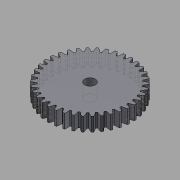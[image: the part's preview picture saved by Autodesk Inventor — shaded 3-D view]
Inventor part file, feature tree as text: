
AUTODESK INVENTOR PART (.ipt)
format: ipt  version: 2015 (Build 190159000, 159)  size: 326,656 bytes
history: native  units: in
note: dims shown in document units (in); Inventor stores cm internally (conversion verified against a paired STEP export)
features: other x13, sketch x3, plane x2
ambient origin geometry x8: Origin, YZ Plane, XZ Plane, XY Plane, X Axis, Y Axis, Z Axis, Center Point
bodies: Solid1 (feature_tree)
feature tree (18):
  other  "Spur Gear2"
  other  "Solid1::Spur Gear2"
  other  "TaggingFeature1"
  sketch  "Sketch1"  dims[d0=0.3937in]
  sketch  "Sketch2"  dims[d16=0.4724in d17=0.0in d41=0.0in d43=0.4724in d46=0.4724in d47=0.0in d48=0.0in]
  sketch  "Sketch3"
  plane  "XZ Plane_1"
  plane  "Work Plane2"
  other  "Z Axis_1"
  other  "Srf1"
  other  "Srf1::Derived"
  other  "Distance iMate"
  other  "Align iMate"
  other  "Mesh iMate"
  other  "Axis iMate"
  other  "Position iMate"
  other  "Mesh iMate2"
  other  "Start plane iMate"
